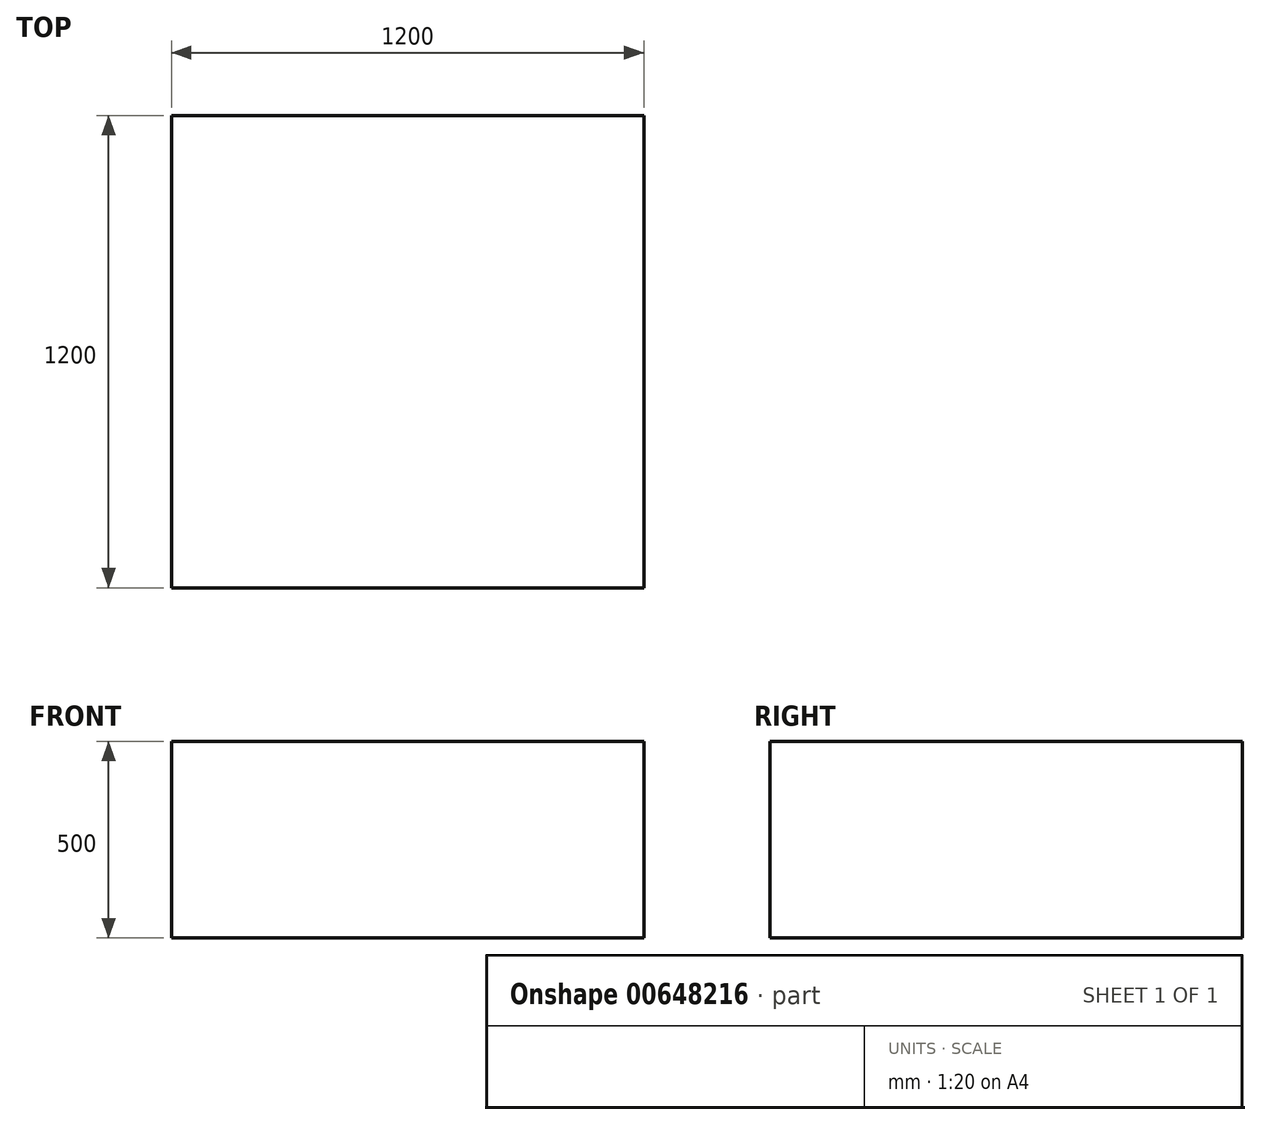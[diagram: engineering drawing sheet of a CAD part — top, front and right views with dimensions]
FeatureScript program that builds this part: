
annotation { "Feature Type Name" : "Feature", "Feature Type Description" : "" }
export const myFeature = defineFeature(function(context is Context, id is Id, definition is map)
    precondition{}
    {
        {
            var Q0;
            Q0=qCreatedBy(makeId("Top.planeOp"),FACE);
            var sketch = newSketch(context, id + "F0", { "sketchPlane" : qUnion([Q0])});
            skLineSegment(sketch, "E0.bottom", {"start": v(600, 599.4) * mm, "end": v(-600, 599.4) * mm});
            skLineSegment(sketch, "E0.top", {"start": v(600, -600.6) * mm, "end": v(-600, -600.6) * mm});
            skLineSegment(sketch, "E0.left", {"start": v(600, 599.4) * mm, "end": v(600, -600.6) * mm});
            skLineSegment(sketch, "E0.right", {"start": v(-600, 599.4) * mm, "end": v(-600, -600.6) * mm});
            skPoint(sketch, "E0.middle", {"position": v(0, -0.6) * mm});
            skSolve(sketch);
        }
        {
            var Q0;
            Q0 = qSketchRegion(id + "F0", true);
            extrude(context, id + "F1", {"entities" : qUnion([Q0]), "depth" : 500 * mm, "offsetDistance" : 25 * mm});
        }
    });
